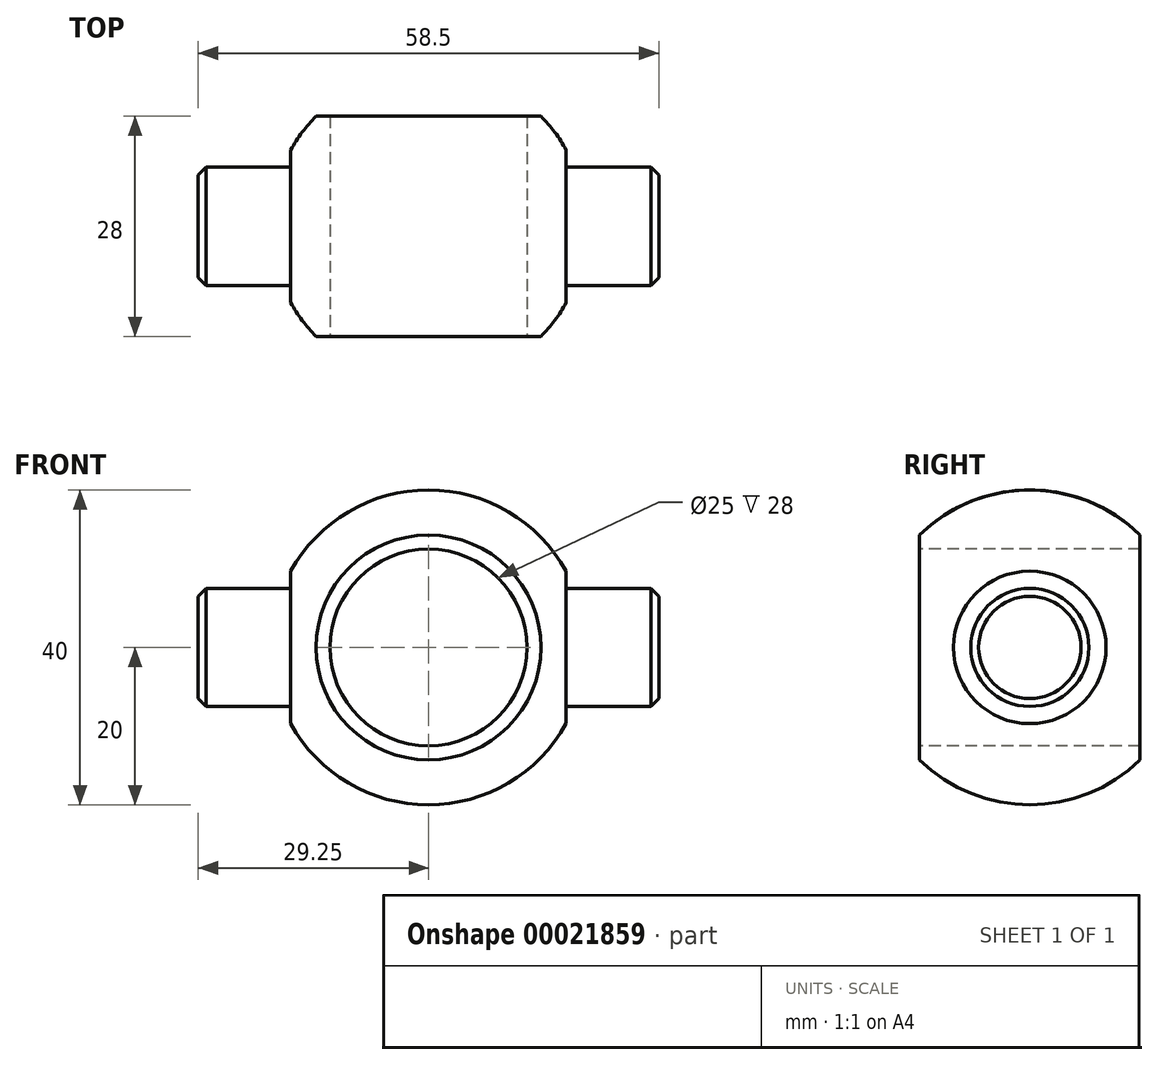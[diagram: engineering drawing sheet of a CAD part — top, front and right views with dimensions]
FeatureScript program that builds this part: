
annotation { "Feature Type Name" : "Feature", "Feature Type Description" : "" }
export const myFeature = defineFeature(function(context is Context, id is Id, definition is map)
    precondition{}
    {
        {
            var Q0;
            Q0=qCreatedBy(makeId("Top.planeOp"),FACE);
            var sketch = newSketch(context, id + "F0", { "sketchPlane" : qUnion([Q0])});
            skArc(sketch, "E0", {"start": v(14.28, -14) * mm, "mid": v(20, 0) * mm, "end": v(14.28, 14) * mm});
            skLineSegment(sketch, "E1", {"start": v(0, 14) * mm, "end": v(0, -14) * mm});
            skLineSegment(sketch, "E2", {"start": v(0, 14) * mm, "end": v(14.28, 14) * mm});
            skLineSegment(sketch, "E3", {"start": v(0, -14) * mm, "end": v(14.28, -14) * mm});
            skSolve(sketch);
        }
        {
            var Q0;
            Q0=makeQuery(id+"F0.imprint","IMPRINT",FACE,{"disambiguationData":[TD([[makeQuery(id+"F0.imprint","IMPRINT",EDGE,{"derivedFrom":sQuery(id+"F0.wireOp",EDGE,"E0")}),1.0]])]});
            var Q1;
            Q1=sQuery(id+"F0.wireOp",EDGE,"E1");
            revolve(context, id + "F1", {"entities" : qUnion([Q0]), "axis" : qUnion([Q1]), "revolveType" : RevolveType.FULL});
        }
        {
            var Q0;
            Q0=qCreatedBy(makeId("Top.planeOp"),FACE);
            var sketch = newSketch(context, id + "F2", { "sketchPlane" : qUnion([Q0])});
            skLineSegment(sketch, "E4.bottom", {"start": v(-56.12, 15) * mm, "end": v(-17.5, 15) * mm});
            skLineSegment(sketch, "E4.top", {"start": v(-56.12, -15) * mm, "end": v(-17.5, -15) * mm});
            skLineSegment(sketch, "E4.left", {"start": v(-56.12, 15) * mm, "end": v(-56.12, -15) * mm});
            skLineSegment(sketch, "E4.right", {"start": v(-17.5, 15) * mm, "end": v(-17.5, -15) * mm});
            skLineSegment(sketch, "E5.bottom", {"start": v(17.5, 15) * mm, "end": v(56.12, 15) * mm});
            skLineSegment(sketch, "E5.top", {"start": v(17.5, -15) * mm, "end": v(56.12, -15) * mm});
            skLineSegment(sketch, "E5.left", {"start": v(17.5, 15) * mm, "end": v(17.5, -15) * mm});
            skLineSegment(sketch, "E5.right", {"start": v(56.12, 15) * mm, "end": v(56.12, -15) * mm});
            skSolve(sketch);
        }
        {
            var Q0;
            Q0=makeQuery(id+"F2.imprint","IMPRINT",FACE,{"disambiguationData":[TD([[makeQuery(id+"F2.imprint","IMPRINT",EDGE,{"derivedFrom":sQuery(id+"F2.wireOp",EDGE,"E4.bottom")}),-1.0]])]});
            var Q1;
            Q1=makeQuery(id+"F2.imprint","IMPRINT",FACE,{"disambiguationData":[TD([[makeQuery(id+"F2.imprint","IMPRINT",EDGE,{"derivedFrom":sQuery(id+"F2.wireOp",EDGE,"E5.bottom")}),-1.0]])]});
            extrude(context, id + "F3", {"entities" : qUnion([Q0, Q1]), "operationType" : NewBodyOperationType.REMOVE, "endBound" : BoundingType.SYMMETRIC, "depth" : 30 * mm});
        }
        {
            var Q0;
            Q0=qCreatedBy(makeId("Right.planeOp"),FACE);
            var sketch = newSketch(context, id + "F4", { "sketchPlane" : qUnion([Q0])});
            skCircle(sketch, "E6", {"center": v(0, 0) * mm, "radius": 7.5 * mm});
            skSolve(sketch);
        }
        {
            var Q0;
            Q0=makeQuery(id+"F4.imprint","IMPRINT",FACE,{"disambiguationData":[TD([[makeQuery(id+"F4.imprint","IMPRINT",EDGE,{"derivedFrom":sQuery(id+"F4.wireOp",EDGE,"E6")}),1.0]])]});
            extrude(context, id + "F5", {"entities" : qUnion([Q0]), "operationType" : NewBodyOperationType.ADD, "endBound" : BoundingType.SYMMETRIC, "depth" : 58.5 * mm});
        }
        {
            var Q0;
            Q0=makeQuery(id+"F1.opRevolve","SWEPT_FACE",FACE,{"disambiguationData":[OSD([sQuery(id+"F0.wireOp",EDGE,"E3")])]});
            var sketch = newSketch(context, id + "F6", { "sketchPlane" : qUnion([Q0])});
            skPoint(sketch, "E7", {"position": v(0, 0) * mm});
            skSolve(sketch);
        }
        {
            var Q0;
            Q0=sQuery(id+"F6.wireOp",VERTEX,"E7");
            var Q1;
            Q1=makeQuery(id+"F1.opRevolve","SWEPT_BODY",BODY,{"disambiguationData":[OSD([sQuery(id+"F0.wireOp",EDGE,"E0"),sQuery(id+"F0.wireOp",EDGE,"E1"),sQuery(id+"F0.wireOp",EDGE,"E2"),sQuery(id+"F0.wireOp",EDGE,"E3")])]});
            hole(context, id + "F7", {"style" : HoleStyle.SIMPLE, "holeDiameter" : 25 * mm, "endStyle" : HoleEndStyle.THROUGH, "locations" : qUnion([Q0]), "scope" : qUnion([Q1])});
        }
        {
            var Q0;
            Q0=makeQuery(id+"F5.opExtrude","CAP_EDGE",EDGE,{"disambiguationData":[OSD([sQuery(id+"F4.wireOp",EDGE,"E6")])],"isStart":true});
            var Q1;
            Q1=makeQuery(id+"F5.opExtrude","CAP_EDGE",EDGE,{"disambiguationData":[OSD([sQuery(id+"F4.wireOp",EDGE,"E6")])],"isStart":false});
            chamfer(context, id + "F8", {"entities" : qUnion([Q0, Q1]), "width" : 1 * mm, "tangentPropagation" : true});
        }
    });
